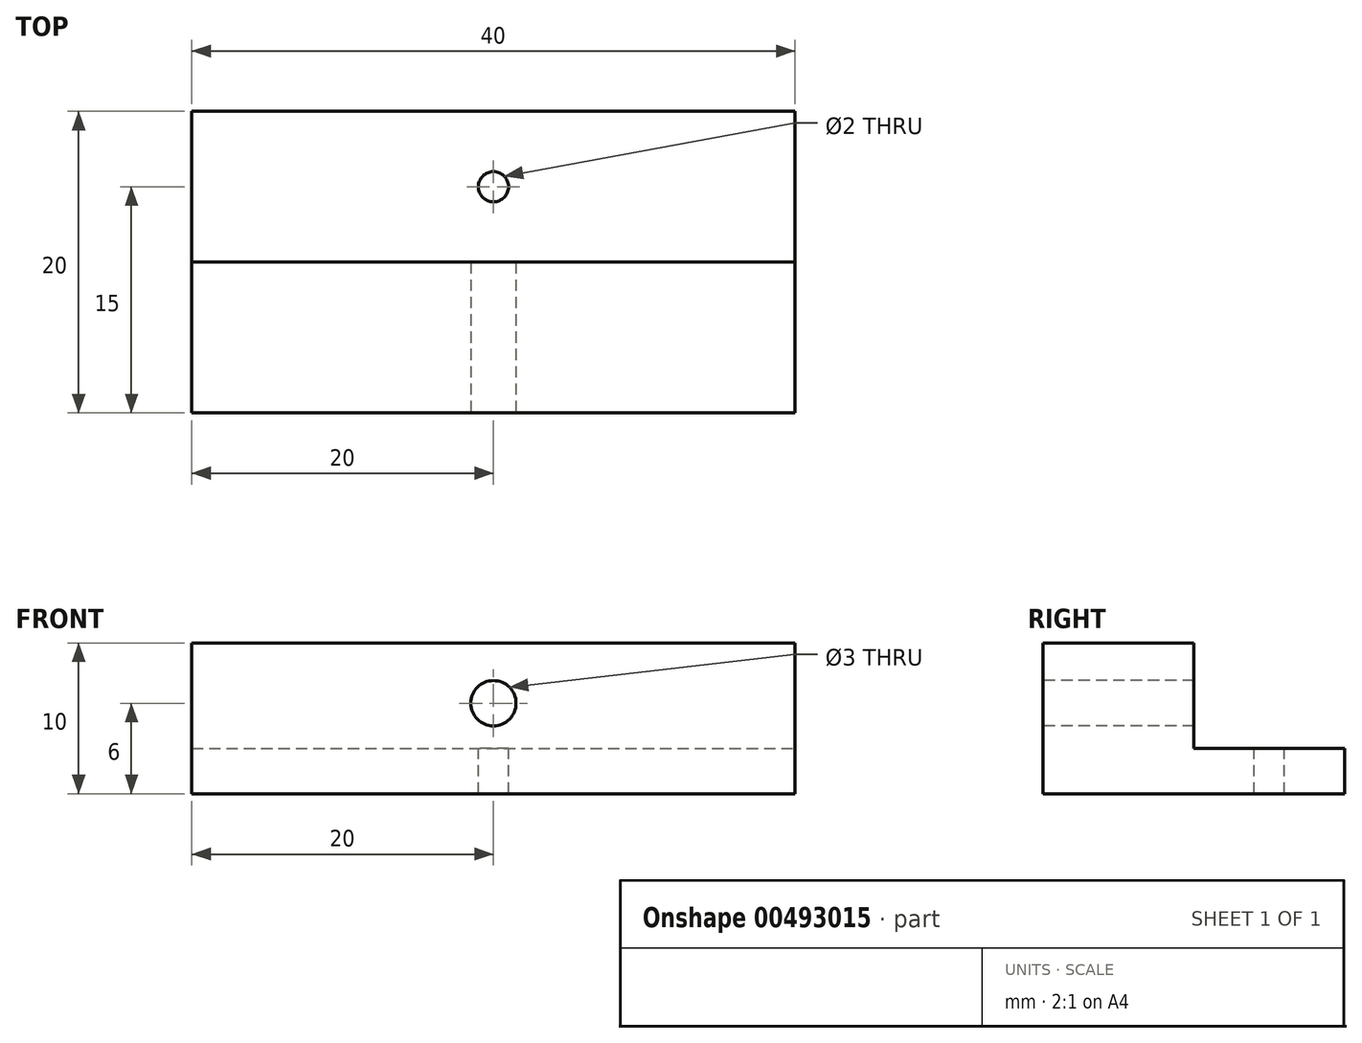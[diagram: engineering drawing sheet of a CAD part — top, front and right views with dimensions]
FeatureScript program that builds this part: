
annotation { "Feature Type Name" : "Feature", "Feature Type Description" : "" }
export const myFeature = defineFeature(function(context is Context, id is Id, definition is map)
    precondition{}
    {
        {
            var Q0;
            Q0=qCreatedBy(makeId("Top.planeOp"),FACE);
            var sketch = newSketch(context, id + "F0", { "sketchPlane" : qUnion([Q0])});
            skLineSegment(sketch, "E0.bottom", {"start": v(-20, 10) * mm, "end": v(20, 10) * mm});
            skLineSegment(sketch, "E0.top", {"start": v(-20, -10) * mm, "end": v(20, -10) * mm});
            skLineSegment(sketch, "E0.left", {"start": v(-20, 10) * mm, "end": v(-20, -10) * mm});
            skLineSegment(sketch, "E0.right", {"start": v(20, 10) * mm, "end": v(20, -10) * mm});
            skSolve(sketch);
        }
        {
            var Q0;
            Q0 = qSketchRegion(id + "F0", true);
            var Q1;
            Q1=sQuery(id+"F0.wireOp",EDGE,"E0.top");
            var Q2;
            Q2=sQuery(id+"F0.wireOp",EDGE,"E0.left");
            var Q3;
            Q3=sQuery(id+"F0.wireOp",EDGE,"E0.right");
            var Q4;
            Q4=sQuery(id+"F0.wireOp",EDGE,"E0.bottom");
            extrude(context, id + "F1", {"entities" : qUnion([Q0]), "surfaceEntities" : qUnion([Q1, Q2, Q3, Q4]), "depth" : 10 * mm});
        }
        {
            var Q0;
            Q0=makeQuery(id+"F1.opExtrude","CAP_FACE",FACE,{"disambiguationData":[OSD([sQuery(id+"F0.wireOp",EDGE,"E0.bottom"),sQuery(id+"F0.wireOp",EDGE,"E0.top"),sQuery(id+"F0.wireOp",EDGE,"E0.left"),sQuery(id+"F0.wireOp",EDGE,"E0.right")])],"isStart":false});
            var sketch = newSketch(context, id + "F2", { "sketchPlane" : qUnion([Q0])});
            skLineSegment(sketch, "E1.bottom", {"start": v(-20, 10) * mm, "end": v(20, 10) * mm});
            skLineSegment(sketch, "E1.top", {"start": v(-20, 0) * mm, "end": v(20, 0) * mm});
            skLineSegment(sketch, "E1.left", {"start": v(-20, 10) * mm, "end": v(-20, 0) * mm});
            skLineSegment(sketch, "E1.right", {"start": v(20, 10) * mm, "end": v(20, 0) * mm});
            skSolve(sketch);
        }
        {
            var Q0;
            Q0 = qSketchRegion(id + "F2", true);
            extrude(context, id + "F3", {"entities" : qUnion([Q0]), "operationType" : NewBodyOperationType.REMOVE, "oppositeDirection" : true, "depth" : 7 * mm});
        }
        {
            var Q0;
            Q0=makeQuery(id+"F1.opExtrude","SWEPT_FACE",FACE,{"disambiguationData":[OSD([sQuery(id+"F0.wireOp",EDGE,"E0.top")])]});
            var sketch = newSketch(context, id + "F4", { "sketchPlane" : qUnion([Q0])});
            skPoint(sketch, "E2", {"position": v(0, 6) * mm});
            skSolve(sketch);
        }
        {
            var Q0;
            Q0=sQuery(id+"F4.wireOp",VERTEX,"E2");
            var Q1;
            Q1=makeQuery(id+"F1.opExtrude","SWEPT_BODY",BODY,{"disambiguationData":[OSD([sQuery(id+"F0.wireOp",EDGE,"E0.bottom"),sQuery(id+"F0.wireOp",EDGE,"E0.top"),sQuery(id+"F0.wireOp",EDGE,"E0.left"),sQuery(id+"F0.wireOp",EDGE,"E0.right")])]});
            hole(context, id + "F5", {"style" : HoleStyle.SIMPLE, "endStyle" : HoleEndStyle.THROUGH, "holeDiameter" : 3 * mm, "isTappedThrough" : true, "tappedDepth" : 12 * mm, "tapClearance" : 3, "locations" : qUnion([Q0]), "scope" : qUnion([Q1])});
        }
        {
            var Q0;
            Q0=makeQuery(id+"F3.boolean.opBoolean","COPY",FACE,{"derivedFrom":makeQuery(id+"F3.opExtrude","CAP_FACE",FACE,{"disambiguationData":[OSD([sQuery(id+"F2.wireOp",EDGE,"E1.bottom"),sQuery(id+"F2.wireOp",EDGE,"E1.top"),sQuery(id+"F2.wireOp",EDGE,"E1.left"),sQuery(id+"F2.wireOp",EDGE,"E1.right")])],"isStart":false})});
            var sketch = newSketch(context, id + "F6", { "sketchPlane" : qUnion([Q0])});
            skPoint(sketch, "E3", {"position": v(0, 5) * mm});
            skSolve(sketch);
        }
        {
            var Q0;
            Q0=sQuery(id+"F6.wireOp",VERTEX,"E3");
            var Q1;
            Q1=makeQuery(id+"F1.opExtrude","SWEPT_BODY",BODY,{"disambiguationData":[OSD([sQuery(id+"F0.wireOp",EDGE,"E0.bottom"),sQuery(id+"F0.wireOp",EDGE,"E0.top"),sQuery(id+"F0.wireOp",EDGE,"E0.left"),sQuery(id+"F0.wireOp",EDGE,"E0.right")])]});
            hole(context, id + "F7", {"style" : HoleStyle.SIMPLE, "endStyle" : HoleEndStyle.THROUGH, "holeDiameter" : 2 * mm, "isTappedThrough" : true, "tappedDepth" : 12 * mm, "tapClearance" : 3, "locations" : qUnion([Q0]), "scope" : qUnion([Q1])});
        }
    });
